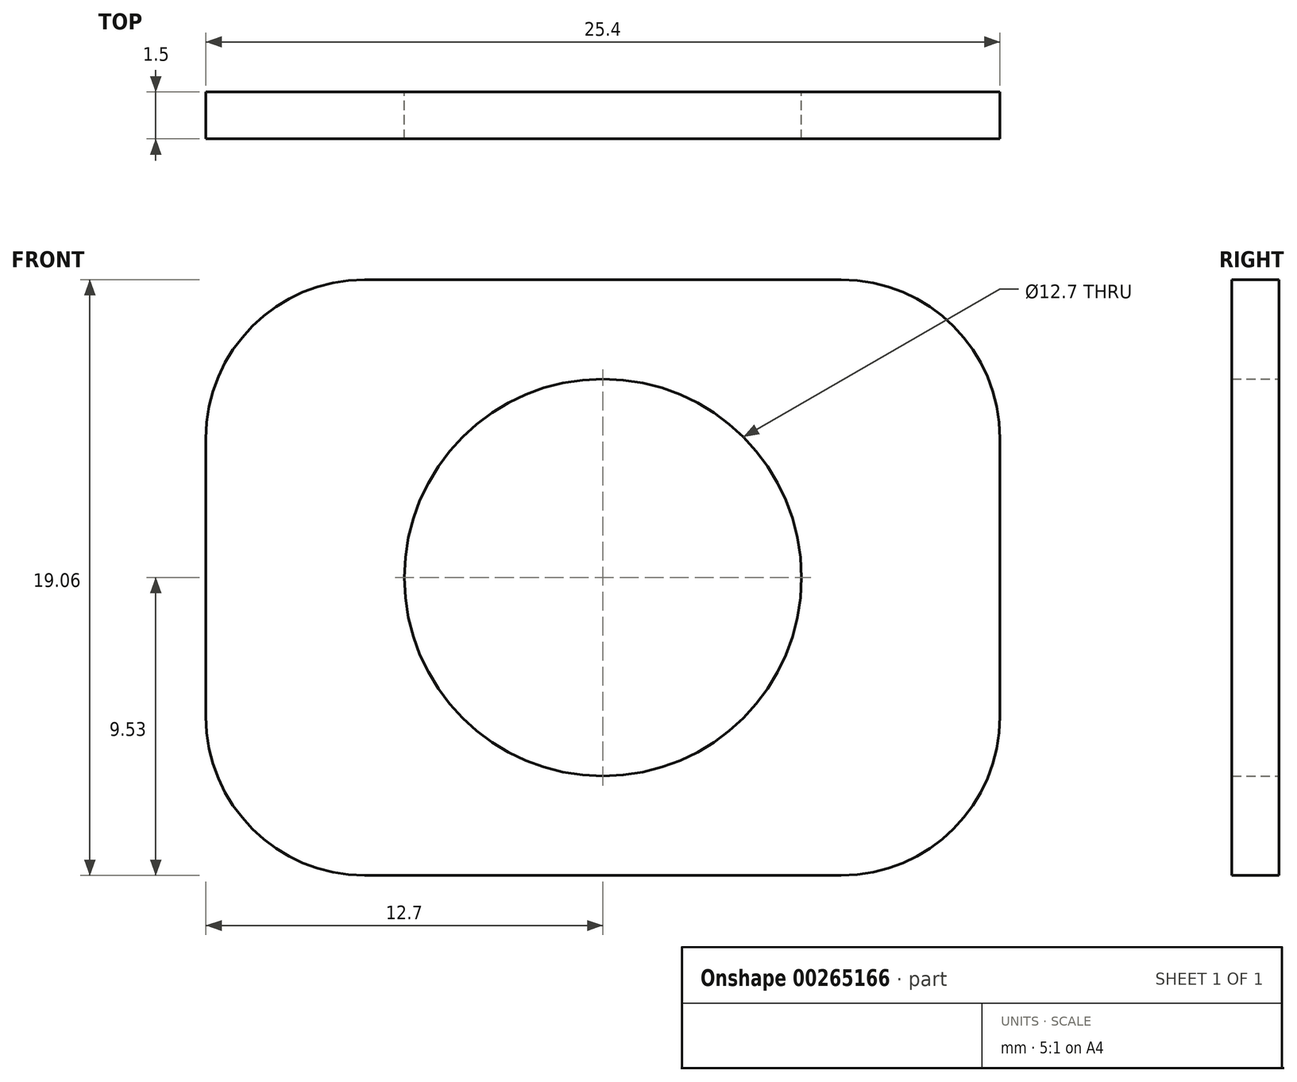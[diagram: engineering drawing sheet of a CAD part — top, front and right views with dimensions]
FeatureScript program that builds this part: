
annotation { "Feature Type Name" : "Feature", "Feature Type Description" : "" }
export const myFeature = defineFeature(function(context is Context, id is Id, definition is map)
    precondition{}
    {
        {
            var Q0;
            Q0=qCreatedBy(makeId("Front.planeOp"),FACE);
            var sketch = newSketch(context, id + "F0", { "sketchPlane" : qUnion([Q0])});
            skCircle(sketch, "E0", {"center": v(0, 0) * mm, "radius": 6.35 * mm});
            skLineSegment(sketch, "E1.bottom", {"start": v(12.7, -9.53) * mm, "end": v(-12.7, -9.53) * mm});
            skLineSegment(sketch, "E1.top", {"start": v(12.7, 9.53) * mm, "end": v(-12.7, 9.52) * mm});
            skLineSegment(sketch, "E1.left", {"start": v(12.7, -9.53) * mm, "end": v(12.7, 9.53) * mm});
            skLineSegment(sketch, "E1.right", {"start": v(-12.7, -9.53) * mm, "end": v(-12.7, 9.52) * mm});
            skSolve(sketch);
        }
        {
            var Q0;
            Q0=makeQuery(id+"F0.imprint","IMPRINT",FACE,{"disambiguationData":[TD([[makeQuery(id+"F0.imprint","IMPRINT",EDGE,{"derivedFrom":sQuery(id+"F0.wireOp",EDGE,"E0")}),-1.0]])]});
            extrude(context, id + "F1", {"entities" : qUnion([Q0]), "depth" : 1.5 * mm});
        }
        {
            var Q0;
            Q0=makeQuery(id+"F1.opExtrude","SWEPT_EDGE",EDGE,{"disambiguationData":[OSD([sQuery(id+"F0.wireOp",EDGE,"E1.bottom"),sQuery(id+"F0.wireOp",EDGE,"E1.right")])]});
            var Q1;
            Q1=makeQuery(id+"F1.opExtrude","SWEPT_EDGE",EDGE,{"disambiguationData":[OSD([sQuery(id+"F0.wireOp",EDGE,"E1.bottom"),sQuery(id+"F0.wireOp",EDGE,"E1.left")])]});
            var Q2;
            Q2=makeQuery(id+"F1.opExtrude","SWEPT_EDGE",EDGE,{"disambiguationData":[OSD([sQuery(id+"F0.wireOp",EDGE,"E1.top"),sQuery(id+"F0.wireOp",EDGE,"E1.left")])]});
            var Q3;
            Q3=makeQuery(id+"F1.opExtrude","SWEPT_EDGE",EDGE,{"disambiguationData":[OSD([sQuery(id+"F0.wireOp",EDGE,"E1.top"),sQuery(id+"F0.wireOp",EDGE,"E1.right")])]});
            fillet(context, id + "F2", {"entities" : qUnion([Q0, Q1, Q2, Q3]), "radius" : 5.08 * mm, "tangentPropagation" : true, "allowEdgeOverflow" : false});
        }
    });
